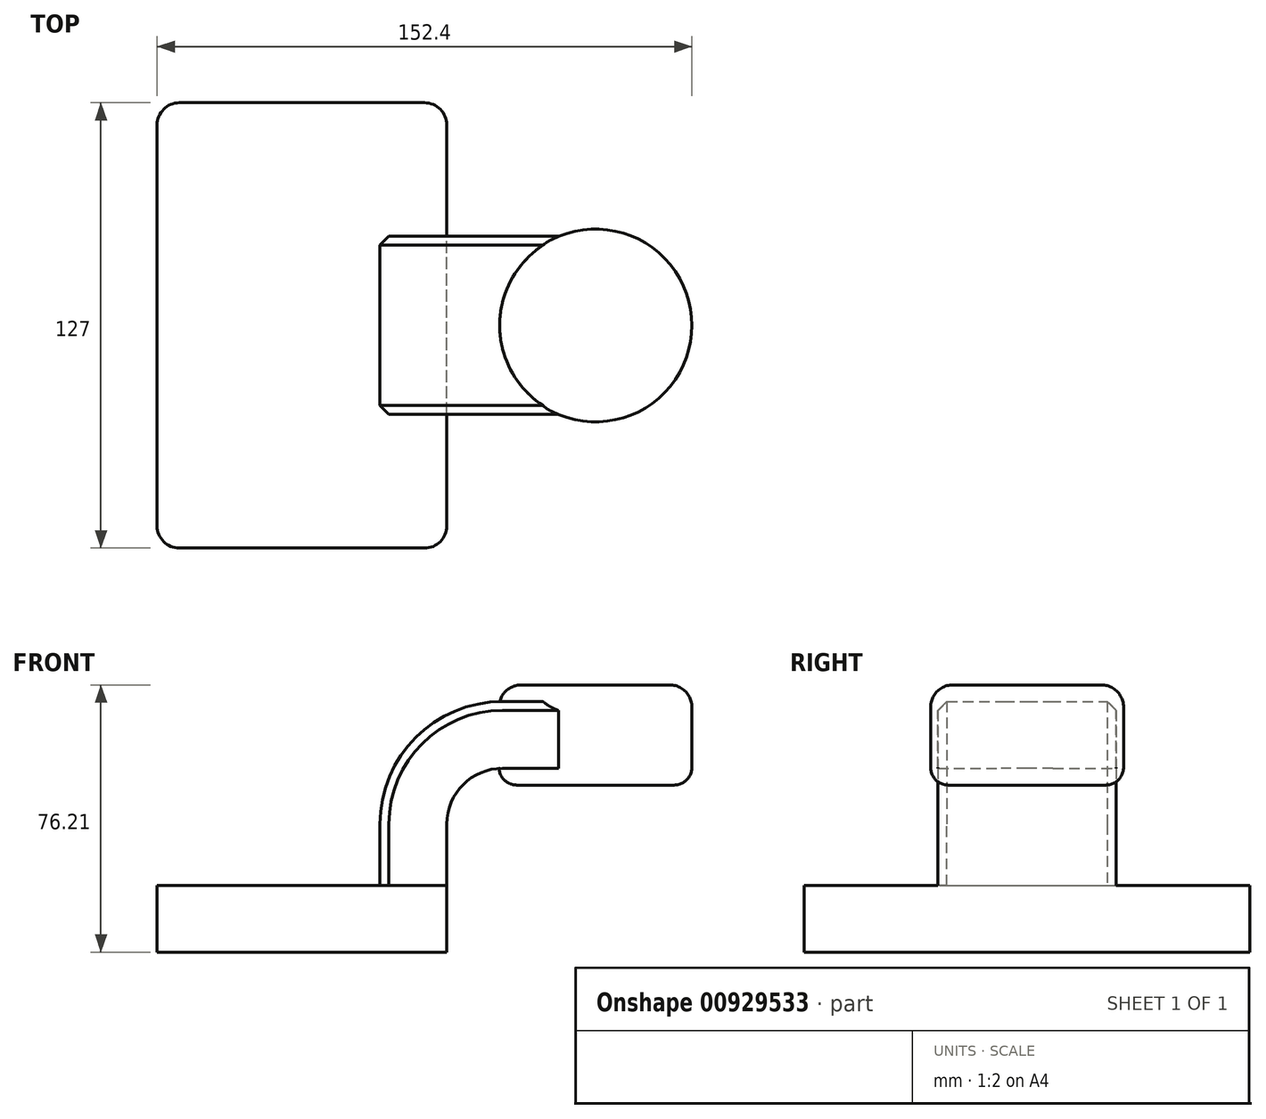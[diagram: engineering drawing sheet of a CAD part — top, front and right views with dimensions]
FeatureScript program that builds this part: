
annotation { "Feature Type Name" : "Feature", "Feature Type Description" : "" }
export const myFeature = defineFeature(function(context is Context, id is Id, definition is map)
    precondition{}
    {
        {
            var Q0;
            Q0=qCreatedBy(makeId("Front.planeOp"),FACE);
            var sketch = newSketch(context, id + "F0", { "sketchPlane" : qUnion([Q0])});
            skLineSegment(sketch, "E0.bottom", {"start": v(41.27, 9.53) * mm, "end": v(-41.28, 9.53) * mm});
            skLineSegment(sketch, "E0.top", {"start": v(41.28, -9.52) * mm, "end": v(-41.27, -9.52) * mm});
            skLineSegment(sketch, "E0.left", {"start": v(41.28, 9.53) * mm, "end": v(41.28, -9.52) * mm});
            skLineSegment(sketch, "E0.right", {"start": v(-41.28, 9.53) * mm, "end": v(-41.27, -9.52) * mm});
            skPoint(sketch, "E0.middle", {"position": v(0, 0) * mm});
            skLineSegment(sketch, "E1.bottom", {"start": v(111.12, 38.1) * mm, "end": v(60.32, 38.1) * mm});
            skLineSegment(sketch, "E1.top", {"start": v(111.12, 66.68) * mm, "end": v(60.32, 66.68) * mm});
            skLineSegment(sketch, "E1.left", {"start": v(111.12, 38.1) * mm, "end": v(111.12, 66.68) * mm});
            skLineSegment(sketch, "E1.right", {"start": v(60.32, 38.1) * mm, "end": v(60.32, 66.68) * mm});
            skPoint(sketch, "E1.middle", {"position": v(85.72, 52.39) * mm});
            skLineSegment(sketch, "E2", {"start": v(41.27, 9.53) * mm, "end": v(41.27, 27) * mm});
            skArc(sketch, "E3", {"start": v(41.27, 27) * mm, "mid": v(45.92, 38.23) * mm, "end": v(57.15, 42.88) * mm});
            skLineSegment(sketch, "E4", {"start": v(57.15, 42.88) * mm, "end": v(83.63, 42.88) * mm});
            skLineSegment(sketch, "E5.0", {"start": v(57.15, 61.93) * mm, "end": v(83.63, 61.93) * mm});
            skArc(sketch, "E5.1", {"start": v(22.22, 27) * mm, "mid": v(32.45, 51.7) * mm, "end": v(57.15, 61.93) * mm});
            skLineSegment(sketch, "E5.2", {"start": v(22.22, 9.53) * mm, "end": v(22.22, 27) * mm});
            skFitSpline(sketch, "E6", {"points": [v(-41.28, 9.53) * mm, v(57.15, 61.93) * mm], "startDerivative": vector(21.82, 124.5) * mm, "endDerivative": vector(153.1, -26.76) * mm});
            skLineSegment(sketch, "E7", {"start": v(83.63, 66.68) * mm, "end": v(83.63, 38.1) * mm});
            skSolve(sketch);
        }
        {
            var Q0;
            Q0=makeQuery(id+"F0.imprint","IMPRINT",FACE,{"disambiguationData":[TD([[makeQuery(id+"F0.imprint","IMPRINT",EDGE,{"derivedFrom":sQuery(id+"F0.wireOp",EDGE,"E0.top")}),-1.0]])]});
            extrude(context, id + "F1", {"entities" : qUnion([Q0]), "endBound" : BoundingType.SYMMETRIC, "depth" : 127 * mm, "offsetDistance" : 25.4 * mm});
        }
        {
            var Q0;
            {var subQ0=sQuery(id+"F0.wireOp",EDGE,"E4");var subQ1=sQuery(id+"F0.wireOp",EDGE,"E1.right");var subQ2=makeQuery(id+"F0.imprint","INTERSECT",VERTEX,{"derivedFrom":[subQ1,subQ0]});Q0=makeQuery(id+"F0.imprint","IMPRINT",FACE,{"disambiguationData":[TD([[makeQuery(id+"F0.imprint","IMPRINT",EDGE,{"disambiguationData":[TD([[subQ2,-1.0]])],"derivedFrom":subQ1}),-1.0]])]});}
            var Q1;
            {var subQ1=sQuery(id+"F0.wireOp",EDGE,"E2");Q1=makeQuery(id+"F0.imprint","IMPRINT",FACE,{"disambiguationData":[TD([[makeQuery(id+"F0.imprint","IMPRINT",EDGE,{"derivedFrom":subQ1}),1.0]])]});}
            extrude(context, id + "F2", {"entities" : qUnion([Q0, Q1]), "operationType" : NewBodyOperationType.ADD, "endBound" : BoundingType.SYMMETRIC, "depth" : 50.8 * mm, "offsetDistance" : 25.4 * mm});
        }
        {
            var Q0;
            Q0=makeQuery(id+"F0.imprint","IMPRINT",FACE,{"disambiguationData":[TD([[makeQuery(id+"F0.imprint","IMPRINT",EDGE,{"derivedFrom":sQuery(id+"F0.wireOp",EDGE,"E5.1")}),1.0]])]});
            extrude(context, id + "F3", {"entities" : qUnion([Q0]), "operationType" : NewBodyOperationType.ADD, "endBound" : BoundingType.SYMMETRIC, "depth" : 15.88 * mm, "offsetDistance" : 25.4 * mm});
        }
        {
            var Q0;
            {var subQ0=sQuery(id+"F0.wireOp",EDGE,"E1.left");Q0=makeQuery(id+"F0.imprint","IMPRINT",FACE,{"disambiguationData":[TD([[makeQuery(id+"F0.imprint","IMPRINT",EDGE,{"derivedFrom":subQ0}),1.0]])]});}
            var Q1;
            Q1=sQuery(id+"F0.wireOp",EDGE,"E7");
            revolve(context, id + "F4", {"operationType" : NewBodyOperationType.ADD, "surfaceOperationType" : NewSurfaceOperationType.NEW, "entities" : qUnion([Q0]), "axis" : qUnion([Q1]), "revolveType" : RevolveType.FULL});
        }
        {
            var Q0;
            Q0=makeQuery(id+"F1.opExtrude","CAP_EDGE",EDGE,{"disambiguationData":[OSD([sQuery(id+"F0.wireOp",EDGE,"E0.left")])],"isStart":false});
            var Q1;
            Q1=makeQuery(id+"F1.opExtrude","CAP_EDGE",EDGE,{"disambiguationData":[OSD([sQuery(id+"F0.wireOp",EDGE,"E0.right")])],"isStart":false});
            var Q2;
            Q2=makeQuery(id+"F1.opExtrude","CAP_EDGE",EDGE,{"disambiguationData":[OSD([sQuery(id+"F0.wireOp",EDGE,"E0.right")])],"isStart":true});
            var Q3;
            Q3=makeQuery(id+"F1.opExtrude","CAP_EDGE",EDGE,{"disambiguationData":[OSD([sQuery(id+"F0.wireOp",EDGE,"E0.left")])],"isStart":true});
            fillet(context, id + "F5", {"entities" : qUnion([Q0, Q1, Q2, Q3]), "radius" : 6.35 * mm, "tangentPropagation" : true, "allowEdgeOverflow" : false});
        }
        {
            var Q0;
            Q0=makeQuery(id+"F3.opExtrude","CAP_EDGE",EDGE,{"disambiguationData":[OSD([sQuery(id+"F0.wireOp",EDGE,"E6")])],"isStart":false});
            var Q1;
            Q1=makeQuery(id+"F3.opExtrude","CAP_EDGE",EDGE,{"disambiguationData":[OSD([sQuery(id+"F0.wireOp",EDGE,"E6")])],"isStart":true});
            var Q2;
            Q2=makeQuery(id+"F2.opExtrude","CAP_EDGE",EDGE,{"disambiguationData":[OSD([sQuery(id+"F0.wireOp",EDGE,"E5.1")])],"isStart":false});
            var Q3;
            Q3=makeQuery(id+"F2.opExtrude","CAP_EDGE",EDGE,{"disambiguationData":[OSD([sQuery(id+"F0.wireOp",EDGE,"E5.1")])],"isStart":true});
            chamfer(context, id + "F6", {"entities" : qUnion([Q0, Q1, Q2, Q3]), "width" : 2.54 * mm, "tangentPropagation" : true});
        }
        {
            var Q0;
            Q0=makeQuery(id+"F4.opRevolve","SWEPT_EDGE",EDGE,{"disambiguationData":[OSD([sQuery(id+"F0.wireOp",EDGE,"E1.top"),sQuery(id+"F0.wireOp",EDGE,"E1.left")])]});
            fillet(context, id + "F7", {"entities" : qUnion([Q0]), "radius" : 6.35 * mm, "tangentPropagation" : true, "allowEdgeOverflow" : false});
        }
        {
            var Q0;
            Q0=makeQuery(id+"F4.opRevolve","SWEPT_EDGE",EDGE,{"disambiguationData":[OSD([sQuery(id+"F0.wireOp",EDGE,"E1.bottom"),sQuery(id+"F0.wireOp",EDGE,"E1.left")])]});
            fillet(context, id + "F8", {"entities" : qUnion([Q0]), "radius" : 5.08 * mm, "tangentPropagation" : true, "allowEdgeOverflow" : false});
        }
    });
